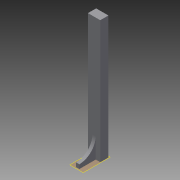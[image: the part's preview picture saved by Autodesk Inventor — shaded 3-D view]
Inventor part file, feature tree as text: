
AUTODESK INVENTOR PART (.ipt)
format: ipt  version: 2015 SP1 (Build 190203100, 203)  size: 131,072 bytes
history: native  units: mm
features: extrude x4, sketch x4, plane x2, reference x2, other x1, fillet x1, pattern_linear x1, projected_geometry x1
ambient origin geometry x8: Origin, YZ Plane, XZ Plane, XY Plane, X Axis, Y Axis, Z Axis, Center Point
bodies: Body1 (feature_tree)
feature tree (16):
  other  "Sólido1"
  extrude  "Extrusión1"  Depth=220.0mm TaperAngle=0.0deg
  extrude  "Extrusión2"  Depth=25.0mm
  plane  "Plano de trabajo1"
  sketch  "Boceto5"  dims[d18=5.0mm d19=2.0mm d20=5.0mm d21=0.0mm]
  plane  "Plano de trabajo2"
  extrude  "Extrusión5"  Depth=2.0mm
  fillet  "Empalme1"  Radius=5.0mm
  extrude  "Extrusión6"  [1 undecoded]
  pattern_linear  "Patrón rectangular1"  [2 undecoded]
  sketch  "Boceto1"  dims[d0=10.0mm d1=0.0mm d2=220.0mm d3=0.0mm]
  reference  "Referencia1"
  sketch  "Boceto2"  dims[d15=10.0mm d16=0.0mm d17=25.0mm]
  reference  "Referencia3"
  sketch  "Boceto6"  dims[d22=220.0mm d24=10.0mm]
  projected_geometry  "Contorno proyectado1"
note: 3 required parameter values undecoded (feature->parameter linkage not recoverable at this tier; creation-order binding heuristic only, values carry confidence <= 0.55)
